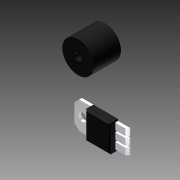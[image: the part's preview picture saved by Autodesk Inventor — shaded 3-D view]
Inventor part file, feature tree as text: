
AUTODESK INVENTOR PART (.ipt)
format: ipt  version: 2012 (Build 160160000, 160)  size: 262,144 bytes
history: native  units: in
note: dims shown in document units (in); Inventor stores cm internally (conversion verified against a paired STEP export)
features: extrude x6, chamfer x3, fillet x2, sketch x1
ambient origin geometry x8: Origin, YZ Plane, XZ Plane, XY Plane, X Axis, Y Axis, Z Axis, Center Point
bodies: Solid1 (feature_tree)
feature tree (12):
  sketch  "Sketch1"  dims[d0=3.2283in d1=2.1654in d2=0.689in d3=1.3976in d4=0.4528in d5=0.0984in d6=0.0394in d7=0.3937in d8=1.0825in d9=0.3543in d10=0.3937in d16=0.2362in d17=0.9in d18=0.7569in d19=0.1in d22=0.027in d24=0.3937in d25=0.1in d26=0.02in d27=0.177in d28=0.177in d29=0.1in d30=0.177in d31=0.02in d32=0.1181in d33=-0.0in d34=0.015in d35=0.125in d36=45.0deg d37=0.0394in d38=0.0in d39=0.07in d40=0.125in d41=45.0deg d42=0.1181in d43=0.0394in d44=0.0in d45=0.0394in d46=0.0in d47=0.035in d48=0.125in d49=45.0deg d50=0.005in d51=0.005in d52=0.1969in d53=0.0in d54=0.3937in d55=0.0in d56=0.0591in d57=0.2953in d58=0.0787in d59=0.0591in d60=0.0591in d61=0.0591in d62=0.0591in d63=0.0591in d64=0.0591in d65=0.0591in d66=0.1in d67=0.1in d68=0.1in d69=0.1in d70=0.1in d71=0.1in d72=0.1in d73=0.0591in d74=0.0591in d75=0.0591in d76=0.0591in d77=0.0591in d78=0.0591in d79=0.0591in d80=0.0591in d81=0.1in d82=0.1in d83=0.1in d84=0.1in d85=0.1in d86=0.1in d87=0.1in d88=0.0787in d89=0.2953in d90=0.0787in d91=0.0787in d92=0.0787in d93=0.0787in d94=0.0787in d95=0.0787in d96=0.0787in d97=0.1969in d98=0.1969in d99=0.1969in d100=0.1969in d101=0.0591in d102=0.0591in d104=0.1969in d105=0.1969in d106=0.0591in d107=0.0591in d108=0.0787in d109=0.0787in d111=0.1969in d112=0.1969in d113=0.1in d114=0.1in d115=0.1969in d116=0.1969in d117=0.1575in d118=0.1in d119=0.1969in d120=0.1969in d121=0.1969in d122=0.1969in d123=0.1969in d124=0.1969in d125=0.1969in d126=0.1969in d127=0.1181in d128=0.1181in d130=0.0394in d131=0.0394in d132=0.0394in d133=0.0394in]
  extrude  "Extrusion1"  Depth=2.1654in
  chamfer  "Chamfer1"  Distance=0.689in
  extrude  "Extrusion2"  Depth=1.3976in
  chamfer  "Chamfer2"  Distance=0.4528in
  extrude  "Extrusion3"  Depth=0.0984in
  extrude  "Extrusion4"  Depth=0.0394in
  chamfer  "Chamfer3"  Distance=0.3937in
  fillet  "Fillet1"  Radius=1.0825in
  fillet  "Fillet2"  Radius=0.3543in
  extrude  "Extrusion5"  Depth=0.3937in
  extrude  "Extrusion6"  Depth=0.2362in
